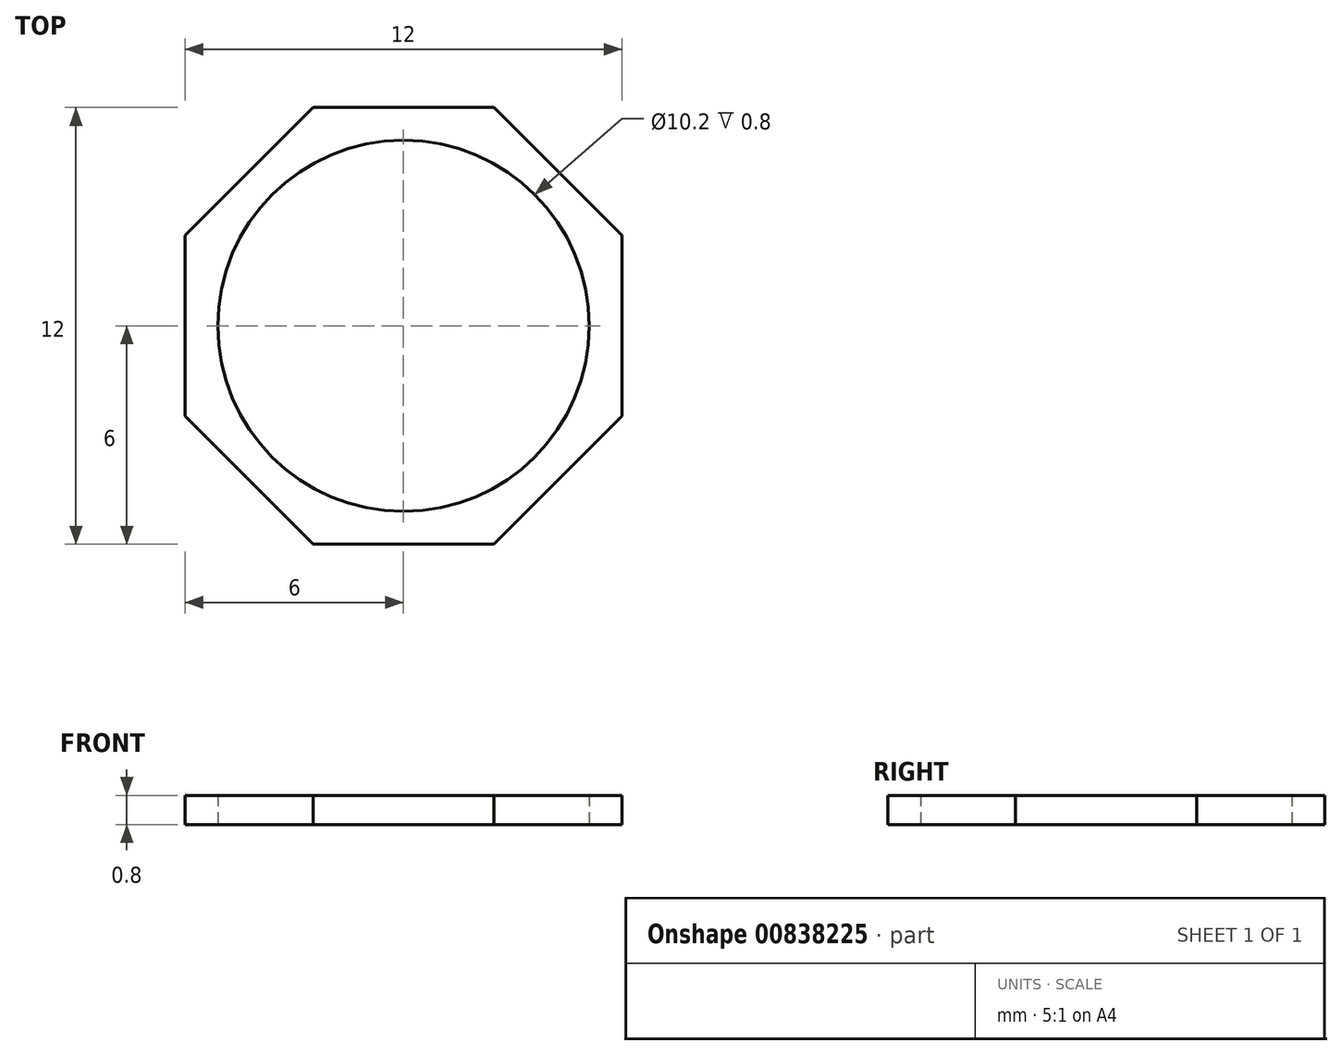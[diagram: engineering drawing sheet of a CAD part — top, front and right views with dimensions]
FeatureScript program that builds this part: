
annotation { "Feature Type Name" : "Feature", "Feature Type Description" : "" }
export const myFeature = defineFeature(function(context is Context, id is Id, definition is map)
    precondition{}
    {
        {
            var Q0;
            Q0=qCreatedBy(makeId("Top.planeOp"),FACE);
            var sketch = newSketch(context, id + "F0", { "sketchPlane" : qUnion([Q0])});
            skCircle(sketch, "E0.cCircle", {"center": v(0, 0) * mm, "radius": 6 * mm, "construction": true});
            skLineSegment(sketch, "E0.0", {"start": v(-2.49, 6) * mm, "end": v(2.49, 6) * mm});
            skLineSegment(sketch, "E0.1", {"start": v(2.49, 6) * mm, "end": v(6, 2.49) * mm});
            skLineSegment(sketch, "E0.2", {"start": v(6, 2.49) * mm, "end": v(6, -2.49) * mm});
            skLineSegment(sketch, "E0.3", {"start": v(6, -2.49) * mm, "end": v(2.49, -6) * mm});
            skLineSegment(sketch, "E0.4", {"start": v(2.49, -6) * mm, "end": v(-2.49, -6) * mm});
            skLineSegment(sketch, "E0.5", {"start": v(-2.49, -6) * mm, "end": v(-6, -2.49) * mm});
            skLineSegment(sketch, "E0.6", {"start": v(-6, -2.49) * mm, "end": v(-6, 2.49) * mm});
            skLineSegment(sketch, "E0.7", {"start": v(-6, 2.49) * mm, "end": v(-2.49, 6) * mm});
            skPoint(sketch, "E0.0.midPoint", {"position": v(0, 6) * mm});
            skCircle(sketch, "E1", {"center": v(0, 0) * mm, "radius": 5.1 * mm});
            skSolve(sketch);
        }
        {
            var Q0;
            Q0=qSketchRegion(id+"F0",true);
            extrude(context, id + "F1", {"entities" : qUnion([Q0]), "depth" : 0.8 * mm, "offsetDistance" : 25 * mm});
        }
    });
